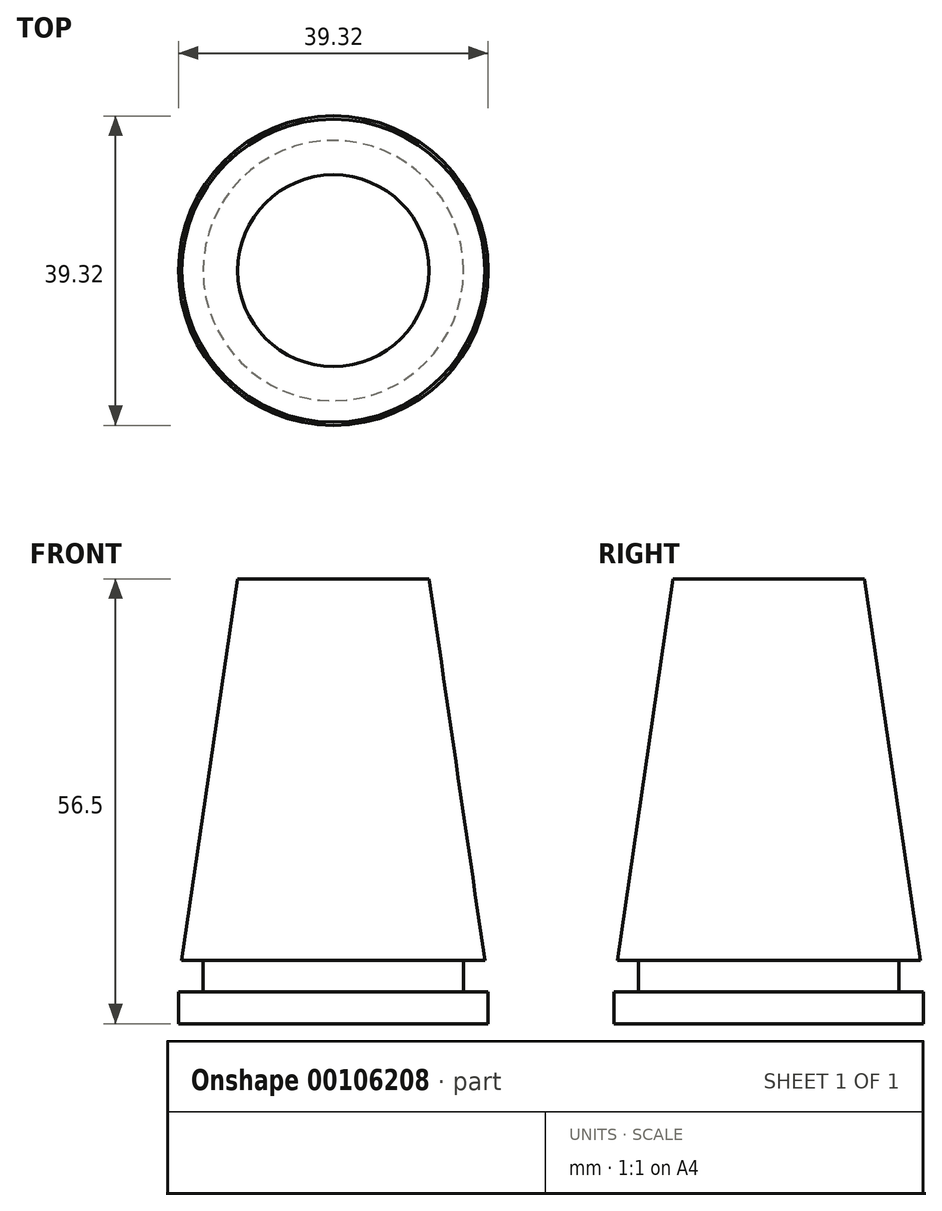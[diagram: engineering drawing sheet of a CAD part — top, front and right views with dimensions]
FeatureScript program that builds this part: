
annotation { "Feature Type Name" : "Feature", "Feature Type Description" : "" }
export const myFeature = defineFeature(function(context is Context, id is Id, definition is map)
    precondition{}
    {
        {
            var Q0;
            Q0=qCreatedBy(makeId("Front.planeOp"),FACE);
            var sketch = newSketch(context, id + "F0", { "sketchPlane" : qUnion([Q0])});
            skLineSegment(sketch, "E0", {"start": v(0, 0) * mm, "end": v(-19.66, 0) * mm});
            skLineSegment(sketch, "E1", {"start": v(-19.66, 0) * mm, "end": v(-19.66, 4.06) * mm});
            skLineSegment(sketch, "E2", {"start": v(-19.66, 4.06) * mm, "end": v(-16.54, 4.06) * mm});
            skLineSegment(sketch, "E3", {"start": v(-16.54, 4.06) * mm, "end": v(-16.54, 8.01) * mm});
            skLineSegment(sketch, "E4", {"start": v(-16.54, 8.01) * mm, "end": v(-19.25, 8.01) * mm});
            skLineSegment(sketch, "E5", {"start": v(-19.25, 8.01) * mm, "end": v(-12.17, 56.5) * mm});
            skLineSegment(sketch, "E6", {"start": v(-12.17, 56.5) * mm, "end": v(0, 56.5) * mm});
            skLineSegment(sketch, "E7", {"start": v(0, 56.5) * mm, "end": v(0, 0) * mm});
            skSolve(sketch);
        }
        {
            var Q0;
            Q0=makeQuery(id+"F0.imprint","IMPRINT",FACE,{"disambiguationData":[TD([[makeQuery(id+"F0.imprint","IMPRINT",EDGE,{"derivedFrom":sQuery(id+"F0.wireOp",EDGE,"E0")}),-1.0]])]});
            var Q1;
            Q1=sQuery(id+"F0.wireOp",EDGE,"E7");
            revolve(context, id + "F1", {"entities" : qUnion([Q0]), "axis" : qUnion([Q1]), "revolveType" : RevolveType.FULL});
        }
    });
